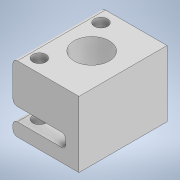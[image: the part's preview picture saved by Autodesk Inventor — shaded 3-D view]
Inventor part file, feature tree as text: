
AUTODESK INVENTOR PART (.ipt)
format: ipt  version: 2020.2 (Build 242310000, 310)  size: 146,432 bytes
history: native  units: mm
features: sketch x3, extrude x2, hole x1, fillet x1
ambient origin geometry x8: Origin, YZ Plane, XZ Plane, XY Plane, X Axis, Y Axis, Z Axis, Center Point
bodies: Solide1 (feature_tree)
feature tree (7):
  extrude  "Extrusion1"  Depth=15.0mm
  hole  "Perçage1"  [1 undecoded]
  extrude  "Extrusion2"  Depth=3.0mm
  fillet  "Congé1"  Radius=9.0mm
  sketch  "Esquisse1"
  sketch  "Esquisse2"
  sketch  "Esquisse3"
note: 1 required parameter value undecoded (feature->parameter linkage not recoverable at this tier; creation-order binding heuristic only, values carry confidence <= 0.55)
